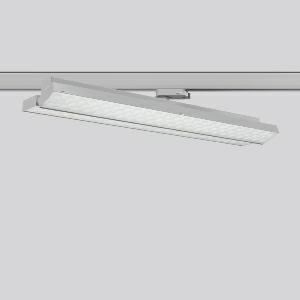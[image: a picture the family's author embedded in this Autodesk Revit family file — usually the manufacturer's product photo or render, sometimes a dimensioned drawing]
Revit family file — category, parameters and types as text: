
# Revit family: tx-move_742161_004_2_76_01f6
name_source: partatom
category: Lighting Fixtures
units: mm (PartAtom-declared; Revit-internal decimal feet)

## family parameters
Cut with Voids When Loaded = No
Host = Face
Light Source = No
Part Type = Normal
Room Calculation Point = No
Round Connector Dimension = Use Diameter
Shared = No

## types (1)
- MultiLumen 1 (1 x LED Modul 927, 2100 lm, 2700)
    Apparent Load = 38 VA
    CIE Flux Codes = 90 97 99 100 100
    Color Rendering = 92
    Color Temperature = 2700
    Default Elevation = 1800 mm
    Description = Series: TX-MOVE
Multifunctional surface-mounted spotlight for area lighting. Very flat design. Housing: sheet steel, powder-coated. Rotation range: 356°. Swivel range: 90°. Consistent alignment possible with visible tilt scale. High-efficiency LED units with optimum light control thanks to clear plastic (PC) lens optics. Spezielle Mikrostrukturen reduzieren Gelbsaum. Symmetrical light distribution. Best colour rendering with CRI >90 for fresh products and coloured textiles. With adapter for RZB 3-circuit DALI tracks. Suitable for Track on ceiling. MultiLumen: Luminous flux adjustable in 3 steps. Factory setting is the highest luminous flux. Environmentally friendly and resource-saving due to replaceable and recyclable components. Very good glare control, ideal for till areas. 
Colour: silver, matt (approx. RAL 9006)
Length: 570 mm
Width: 119 mm
Height: 88 mm
Lamp: LED
Socket: without socket
Colour temperature: 2700K
Colour rendering index (CRI): 90
System power: 38 W
Rated luminous flux: 4200 lm
Luminous efficiency: 111 lm/W
System power 2: 51 W
Rated luminous flux 2: 5500 lm
Luminous efficiency 2: 108 lm/W
System power 3: 62 W
Rated luminous flux 3: 6500 lm
Luminous efficiency 3: 105 lm/W
Control gear: Dimmable EVG, DALI
Protection class: I
Type of protection: IP 20
    Height = 75 mm
    Lamp = 1 x LED Modul 927
    Lamp Light Flux = 2100 lm
    Lamp count = 1
    Length = 569 mm
    Lifetime = 50000 h
    Luminous efficacy = 111 lm/W
    Manufacturer = RZB
    ModVariant = No
    Model = 742161.004.2.76
    Mounting Place = Ceiling
    Mounting Type = Surface mounted
    Number of Poles = 1
    OnlyDefault = Yes
    Power Factor = 1
    Product Name = TX-MOVE
    Product group = Track mounted projectors
    ProductGroupID = 301
    Protection Class = Protection class I
    Protection Degree = IP 20
    RLX_Detail_Level = 1
    RLX_Emergency_Light_Flux = 0 lm
    RLX_Emergency_Type = 0
    RLX_Emergency_Type_DB = No
    RlxData = <blob elided: 33365 chars, md5=78b0f1a1>
    Socket = socket
    Standby Power = 0 W
    System Light Flux = 4200 lm
    System Power = 38 W
    Type Comments = MultiLumen 1
    Type Image = 742162.004.jpg
    URL = http://relux.com
    VarID = multilumen_1
    Voltage = 0 V
    Weight = 0.00 kg
    Width = 119 mm

## geometry (parser evidence)
native form markers: Blend x4, Sweep x14
no freeform markers — native parametric forms only
